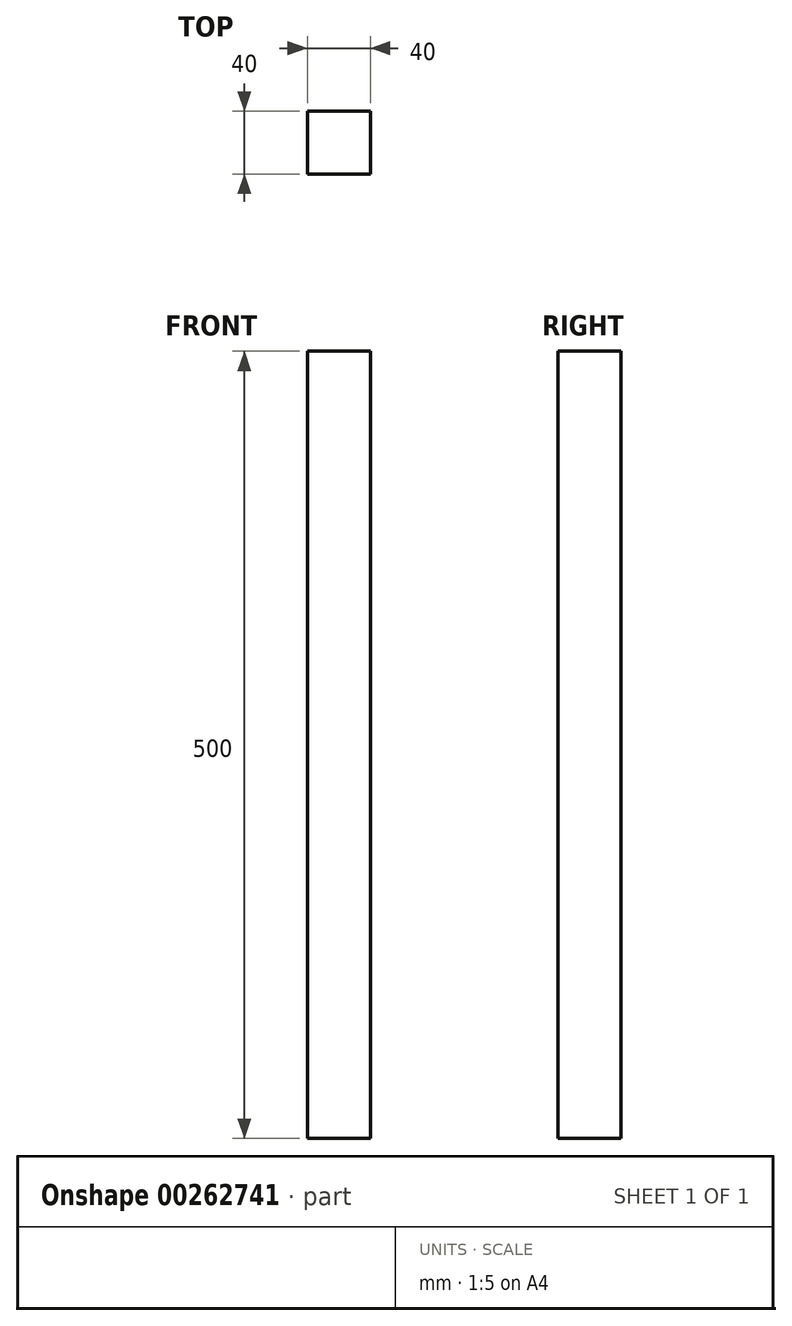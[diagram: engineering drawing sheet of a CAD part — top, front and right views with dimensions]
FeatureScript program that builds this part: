
annotation { "Feature Type Name" : "Feature", "Feature Type Description" : "" }
export const myFeature = defineFeature(function(context is Context, id is Id, definition is map)
    precondition{}
    {
        {
            var Q0;
            Q0=qCreatedBy(makeId("Top.planeOp"),FACE);
            var sketch = newSketch(context, id + "F0", { "sketchPlane" : qUnion([Q0])});
            skLineSegment(sketch, "E0.bottom", {"start": v(0, 0) * mm, "end": v(40, 0) * mm});
            skLineSegment(sketch, "E0.top", {"start": v(0, 40) * mm, "end": v(40, 40) * mm});
            skLineSegment(sketch, "E0.left", {"start": v(0, 0) * mm, "end": v(0, 40) * mm});
            skLineSegment(sketch, "E0.right", {"start": v(40, 0) * mm, "end": v(40, 40) * mm});
            skSolve(sketch);
        }
        {
            var Q0;
            Q0 = qSketchRegion(id + "F0", true);
            extrude(context, id + "F1", {"entities" : qUnion([Q0]), "depth" : 500 * mm});
        }
    });
